# Revit family: QF_COMCATER ALL BRANDS_RCSPR6
name_source: partatom
category: Specialty Equipment
revit_build: Autodesk Revit 2014 (Build: 20140709_2115(x64)
units: mm (PartAtom-declared; Revit-internal decimal feet)

## types (1)
- RCSPR6
    Accessory = No
    Assembly Code = E1090320
    Depth Actual = 803 mm  [stored 2.63451 ft]
    Description = 600 MM WIDE INFILL BENCH
    Height Actual = 910 mm
    Length Actual = 600 mm
    Manufacturer = TRUEHEAT
    Model = RCSPR6
    Type Comments = The Australian owned and designed* Trueheat RC Series of Gas Cooking Equipment has been developed for the restaurant and cafe market with a high quality finish, designed to fulfill the busy demands within a commercial kitchen.
Sturdy range matched infill benches with stand.
Note: Legs, feet and shelf can be removed to allow infill bench to be suspended between units on either side. (Hardware not included).

note: [stored X ft] marks values corroborated as IEEE doubles in the binary element streams (Revit-internal decimal feet)

## geometry (parser evidence)
native form markers: Sweep x3
no freeform markers — native parametric forms only
